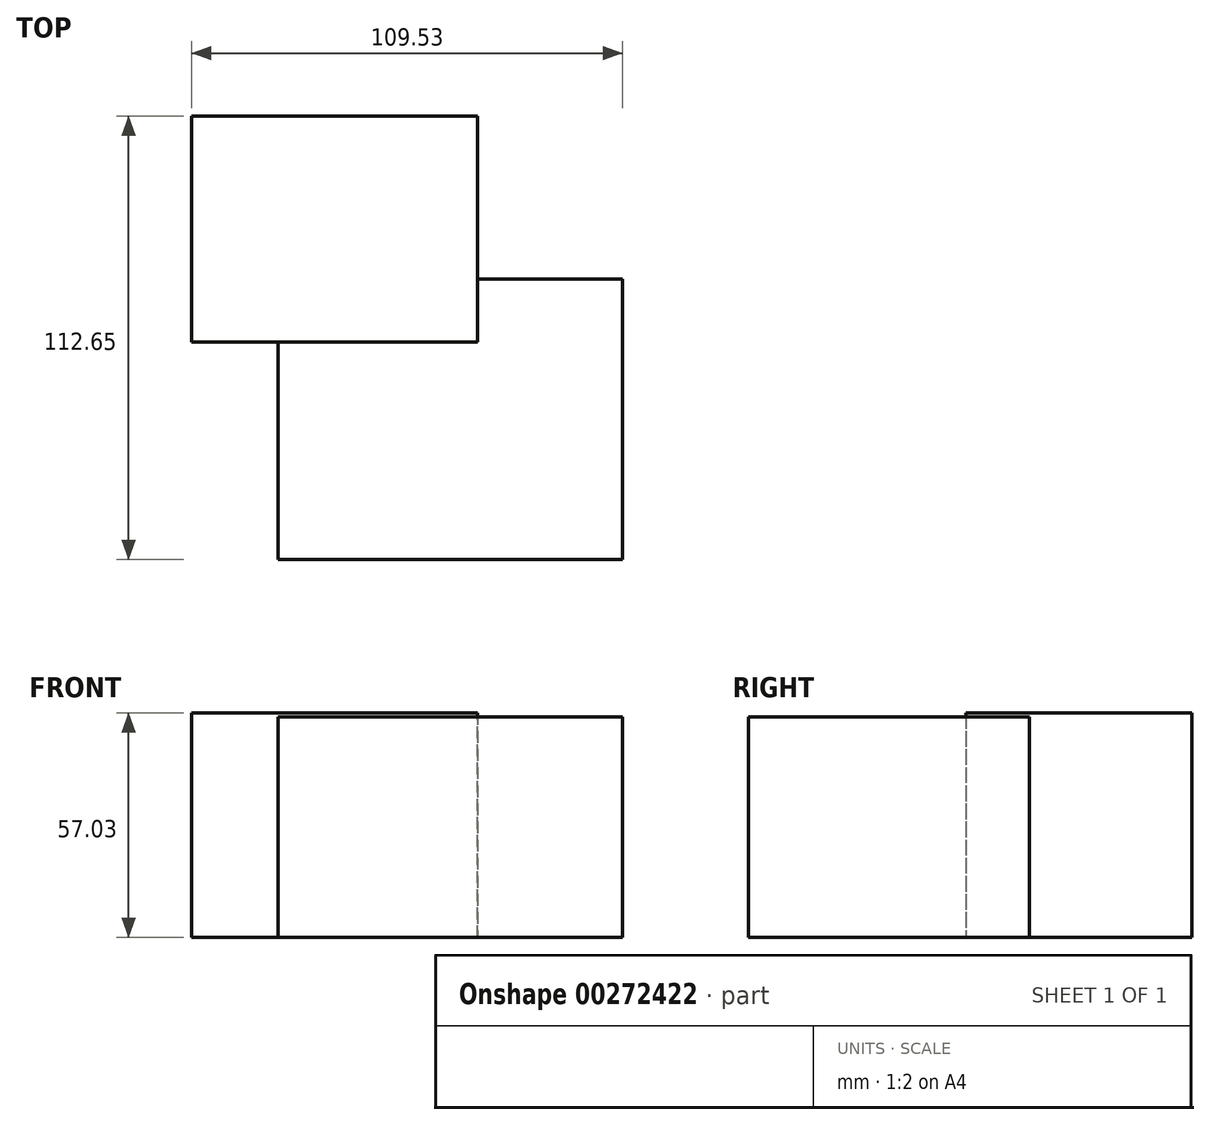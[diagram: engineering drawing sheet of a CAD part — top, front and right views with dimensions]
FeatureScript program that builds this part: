
annotation { "Feature Type Name" : "Feature", "Feature Type Description" : "" }
export const myFeature = defineFeature(function(context is Context, id is Id, definition is map)
    precondition{}
    {
        {
            var Q0;
            Q0=qCreatedBy(makeId("Top.planeOp"),FACE);
            var sketch = newSketch(context, id + "F0", { "sketchPlane" : qUnion([Q0])});
            skLineSegment(sketch, "E0.bottom", {"start": v(-89.15, 71.8) * mm, "end": v(-16.5, 71.8) * mm});
            skLineSegment(sketch, "E0.top", {"start": v(-89.15, 14.33) * mm, "end": v(-16.5, 14.33) * mm});
            skLineSegment(sketch, "E0.left", {"start": v(-89.15, 71.8) * mm, "end": v(-89.15, 14.33) * mm});
            skLineSegment(sketch, "E0.right", {"start": v(-16.5, 71.8) * mm, "end": v(-16.5, 14.33) * mm});
            skSolve(sketch);
        }
        {
            var Q0;
            Q0 = qSketchRegion(id + "F0", true);
            var Q1;
            Q1 = qSketchRegion(id + "F4", true);
            extrude(context, id + "F1", {"entities" : qUnion([Q0, Q1]), "depth" : 57.03 * mm});
        }
        {
            var Q0;
            Q0=qCreatedBy(makeId("Top.planeOp"),FACE);
            var sketch = newSketch(context, id + "F2", { "sketchPlane" : qUnion([Q0])});
            skLineSegment(sketch, "E1.bottom", {"start": v(-67.18, 30.44) * mm, "end": v(20.38, 30.44) * mm});
            skLineSegment(sketch, "E1.top", {"start": v(-67.18, -40.86) * mm, "end": v(20.38, -40.86) * mm});
            skLineSegment(sketch, "E1.left", {"start": v(-67.18, 30.44) * mm, "end": v(-67.18, -40.86) * mm});
            skLineSegment(sketch, "E1.right", {"start": v(20.38, 30.44) * mm, "end": v(20.38, -40.86) * mm});
            skSolve(sketch);
        }
        {
            var Q0;
            Q0 = qSketchRegion(id + "F2", true);
            extrude(context, id + "F3", {"entities" : qUnion([Q0]), "operationType" : NewBodyOperationType.ADD, "depth" : 56 * mm});
        }
    });
